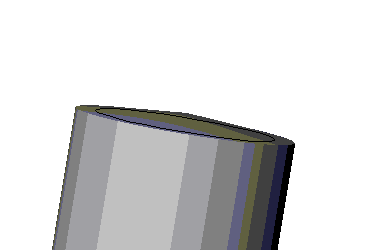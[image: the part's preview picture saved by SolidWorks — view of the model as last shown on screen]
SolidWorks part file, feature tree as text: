
SOLIDWORKS PART (.sldprt)
format: sldprt  version: not decoded by parser v0  size: 183,808 bytes
history: native  units: mm
features: sketch x8, extrude x5, plane x3, thread x2, hole x1, revolve x1 + 1 further entry (+6 scaffold rows collapsed)
feature tree (27):
  scaffold x6  (default folders/planes/origin — collapsed)
  "Corps de surface"
  plane  "Plan1"
  plane  "Plan2"
  plane  "Plan3"
  sketch  "Esquisse1"  dims[D1=25.0mm]
  extrude  "Base-Extrusion"  Depth=281mm
  sketch  "Esquisse2"  dims[D1=23.0mm]
  extrude  "Boss.-Extru.1"  Depth=10mm
  sketch  "Esquisse3"  dims[D1=18.0mm]
  extrude  "Boss.-Extru.2"  Depth=3mm
  sketch  "Esquisse4"  dims[D1=22.0mm]
  extrude  "Boss.-Extru.3"  [1 undecoded]
  thread  "Représentation de filetage2"  Diameter=36mm  [1 undecoded]
  sketch  "Esquisse5"  dims[D1=12.0mm]
  extrude  "Boss.-Extru.4"  Depth=37mm
  hole  "Perçage1"  Diameter=8mm Depth=40mm
  sketch  "Esquisse7"
  sketch  "Esquisse6"  dims[c1.D1=~97.659253deg c1.D2=~82.982399deg c1.Diamètre=8.0mm c2.D2=100.0mm c2.D3=~82.982399deg c2.D4=90.0deg c3.D3=~97.716715deg c3.Profondeur=40.0mm c3.Angle=118.0deg]
  thread  "Représentation de filetage4"  Diameter=36mm  [1 undecoded]
  sketch  "Esquisse8"
  revolve  "Révolution1"  Angle=360deg
decode coverage: 14 of 17 modeling features carry decoded parameters; 1 rows unclassified (native names shown)
note: ~ marks probable driven/reference dimensions
note: 3 parameter values undecoded
note: suppression state not decoded; provenance and decode notes live in map.json
